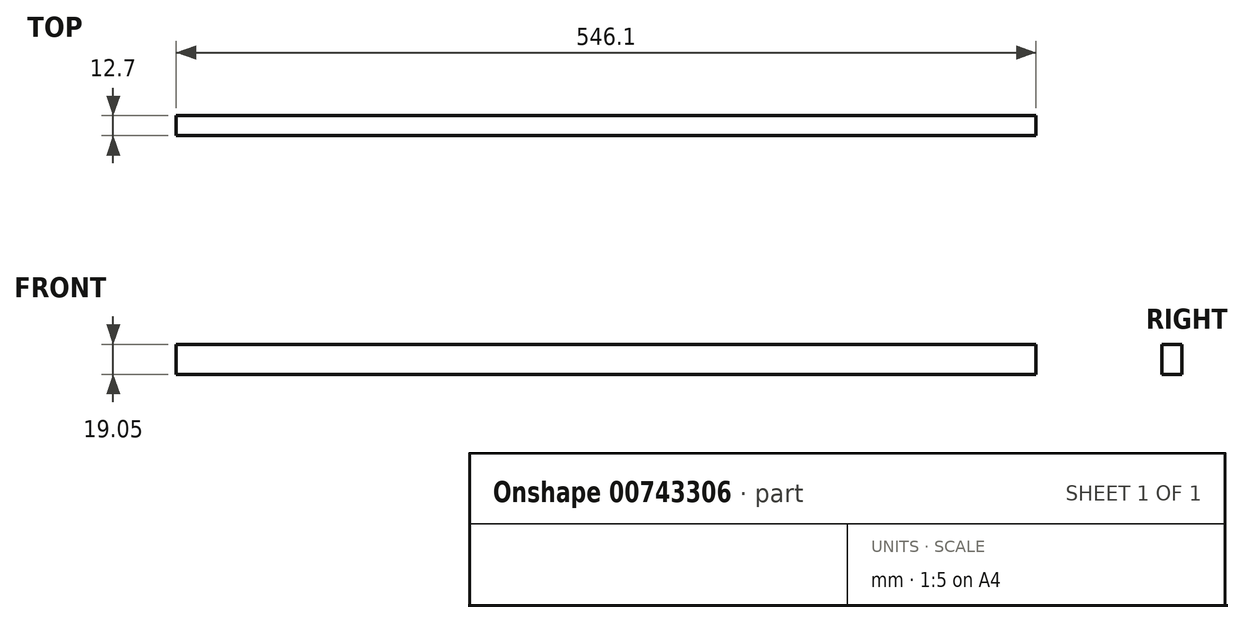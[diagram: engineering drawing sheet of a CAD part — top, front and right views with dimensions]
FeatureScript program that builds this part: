
annotation { "Feature Type Name" : "Feature", "Feature Type Description" : "" }
export const myFeature = defineFeature(function(context is Context, id is Id, definition is map)
    precondition{}
    {
        {
            var Q0;
            Q0=qCreatedBy(makeId("Front.planeOp"),FACE);
            var sketch = newSketch(context, id + "F0", { "sketchPlane" : qUnion([Q0])});
            skLineSegment(sketch, "E0.bottom", {"start": v(-76.14, 12.05) * mm, "end": v(469.96, 12.05) * mm});
            skLineSegment(sketch, "E0.top", {"start": v(-76.14, -7) * mm, "end": v(469.96, -7) * mm});
            skLineSegment(sketch, "E0.left", {"start": v(-76.14, 12.05) * mm, "end": v(-76.14, -7) * mm});
            skLineSegment(sketch, "E0.right", {"start": v(469.96, 12.05) * mm, "end": v(469.96, -7) * mm});
            skSolve(sketch);
        }
        {
            var Q0;
            Q0=makeQuery(id+"F0.imprint","IMPRINT",FACE,{"disambiguationData":[TD([[makeQuery(id+"F0.imprint","IMPRINT",EDGE,{"derivedFrom":sQuery(id+"F0.wireOp",EDGE,"E0.bottom")}),-1.0]])]});
            extrude(context, id + "F1", {"entities" : qUnion([Q0]), "depth" : 12.7 * mm, "offsetDistance" : 25.4 * mm});
        }
    });
